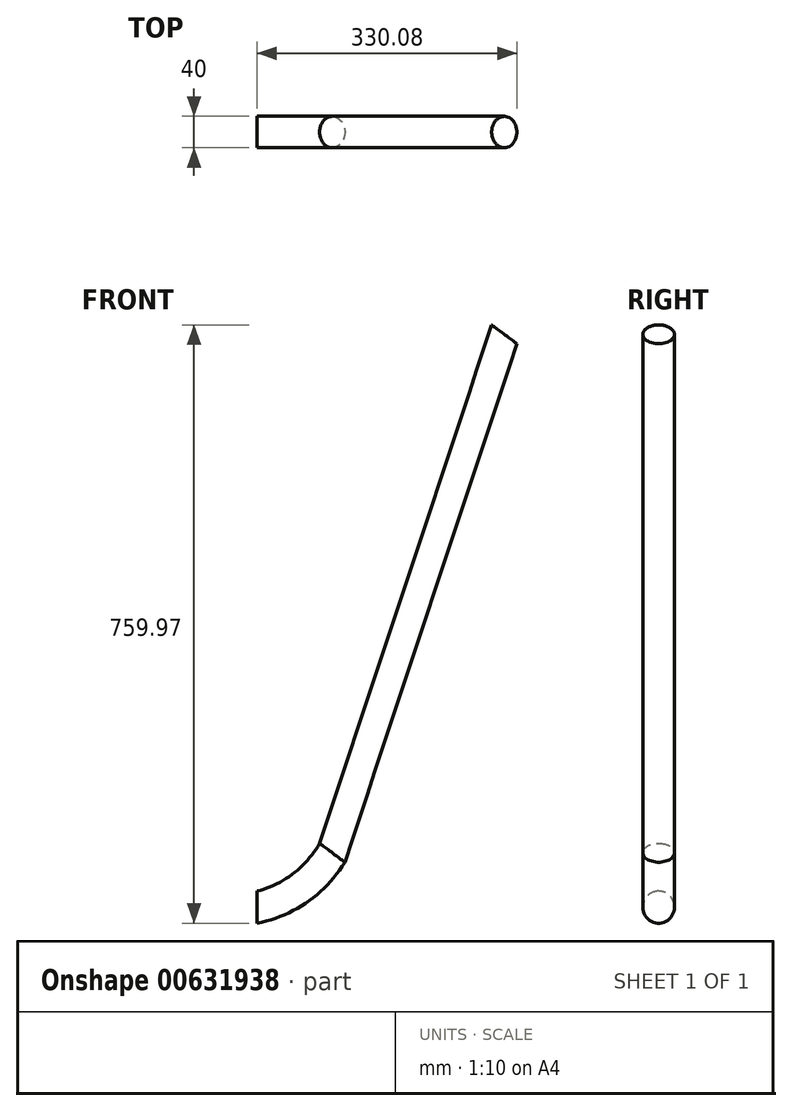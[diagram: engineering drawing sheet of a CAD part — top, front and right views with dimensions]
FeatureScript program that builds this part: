
annotation { "Feature Type Name" : "Feature", "Feature Type Description" : "" }
export const myFeature = defineFeature(function(context is Context, id is Id, definition is map)
    precondition{}
    {
        {
            var Q0;
            Q0=qCreatedBy(makeId("Front.planeOp"),FACE);
            var sketch = newSketch(context, id + "F0", { "sketchPlane" : qUnion([Q0])});
            skLineSegment(sketch, "E0", {"start": v(152.56, -358.45) * mm, "end": v(-66.07, 300.12) * mm});
            skLineSegment(sketch, "E1", {"start": v(200.01, -392.7) * mm, "end": v(207.84, -392.7) * mm});
            skLineSegment(sketch, "E2", {"start": v(255.3, -358.45) * mm, "end": v(473.93, 300.12) * mm});
            skPoint(sketch, "E3.visualSharp", {"position": v(163.93, -392.7) * mm});
            skArc(sketch, "E3.filletArc", {"start": v(152.56, -358.45) * mm, "mid": v(170.75, -383.24) * mm, "end": v(200.01, -392.7) * mm});
            skPoint(sketch, "E4.visualSharp", {"position": v(243.93, -392.7) * mm});
            skArc(sketch, "E4.filletArc", {"start": v(207.84, -392.7) * mm, "mid": v(237.1, -383.24) * mm, "end": v(255.3, -358.45) * mm});
            skSolve(sketch);
        }
        {
            var Q0;
            Q0=qCreatedBy(makeId("Top.planeOp"),FACE);
            var sketch = newSketch(context, id + "F1", { "sketchPlane" : qUnion([Q0])});
            skCircle(sketch, "E5", {"center": v(-66.08, 0) * mm, "radius": 20 * mm});
            skSolve(sketch);
        }
        {
            var Q0;
            Q0=makeQuery(id+"F1.imprint","IMPRINT",FACE,{"disambiguationData":[TD([[makeQuery(id+"F1.imprint","IMPRINT",EDGE,{"derivedFrom":sQuery(id+"F1.wireOp",EDGE,"E5")}),1.0]])]});
            var Q1;
            Q1=sQuery(id+"F0.wireOp",EDGE,"E4.filletArc");
            var Q2;
            Q2=sQuery(id+"F0.wireOp",EDGE,"E1");
            var Q3;
            Q3=sQuery(id+"F0.wireOp",EDGE,"E3.filletArc");
            var Q4;
            Q4=sQuery(id+"F0.wireOp",EDGE,"E0");
            var Q5;
            Q5=sQuery(id+"F0.wireOp",EDGE,"E2");
            sweep(context, id + "F2", {"profiles" : qUnion([Q0]), "path" : qUnion([Q1, Q2, Q3, Q4, Q5])});
        }
        {
            var Q0;
            Q0=qCreatedBy(makeId("Front.planeOp"),FACE);
            cPlane(context, id + "F3", {"entities" : qUnion([Q0]), "cplaneType" : CPlaneType.OFFSET, "offset" : 31 * mm, "width" : 150 * mm, "height" : 150 * mm});
        }
        {
            var Q0;
            Q0=qCreatedBy(id+"F3.planeOp",FACE);
            var sketch = newSketch(context, id + "F4", { "sketchPlane" : qUnion([Q0])});
            skLineSegment(sketch, "E6.bottom", {"start": v(-252.42, 323.14) * mm, "end": v(239.73, 323.14) * mm});
            skLineSegment(sketch, "E6.top", {"start": v(-252.42, -580.81) * mm, "end": v(239.73, -580.81) * mm});
            skLineSegment(sketch, "E6.left", {"start": v(-252.42, 323.14) * mm, "end": v(-252.42, -580.81) * mm});
            skLineSegment(sketch, "E6.right", {"start": v(239.73, 323.14) * mm, "end": v(239.73, -580.81) * mm});
            skSolve(sketch);
        }
        {
            var Q0;
            Q0=makeQuery(id+"F4.imprint","IMPRINT",FACE,{"disambiguationData":[TD([[makeQuery(id+"F4.imprint","IMPRINT",EDGE,{"derivedFrom":sQuery(id+"F4.wireOp",EDGE,"E6.bottom")}),-1.0]])]});
            extrude(context, id + "F5", {"entities" : qUnion([Q0]), "operationType" : NewBodyOperationType.REMOVE, "oppositeDirection" : true, "depth" : 285 * mm, "offsetDistance" : 25 * mm});
        }
    });
